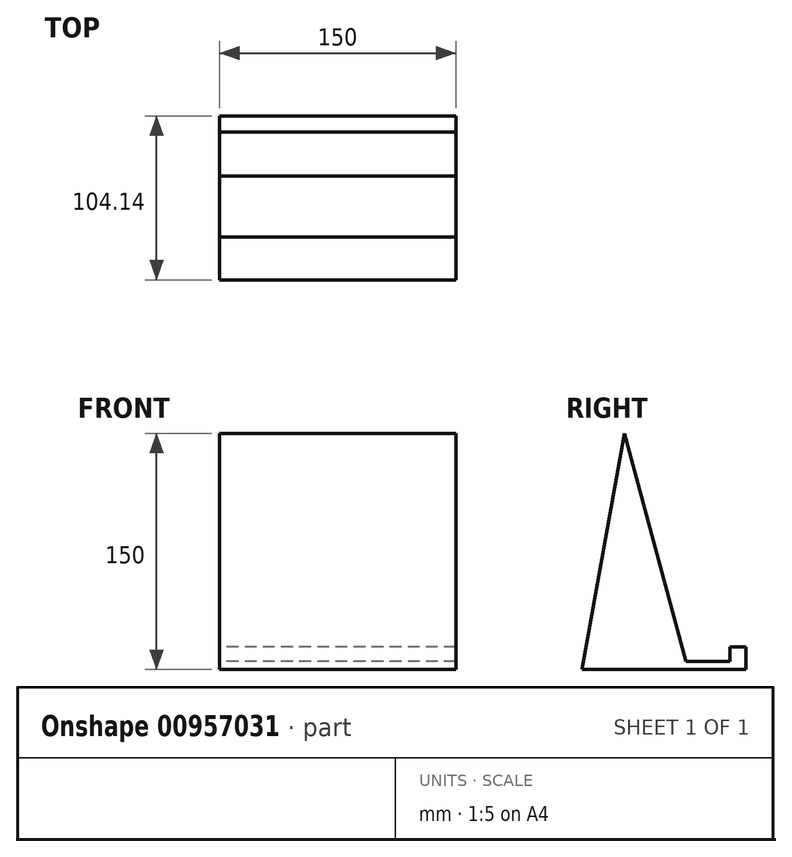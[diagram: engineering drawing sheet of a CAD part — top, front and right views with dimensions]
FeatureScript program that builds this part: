
annotation { "Feature Type Name" : "Feature", "Feature Type Description" : "" }
export const myFeature = defineFeature(function(context is Context, id is Id, definition is map)
    precondition{}
    {
        {
            var Q0;
            Q0=qCreatedBy(makeId("Right.planeOp"),FACE);
            var sketch = newSketch(context, id + "F0", { "sketchPlane" : qUnion([Q0])});
            skLineSegment(sketch, "E0", {"start": v(0, 150) * mm, "end": v(-27.16, 0) * mm});
            skLineSegment(sketch, "E1", {"start": v(-27.16, 0) * mm, "end": v(40.2, 0) * mm});
            skLineSegment(sketch, "E2", {"start": v(38.82, 5.11) * mm, "end": v(0, 150) * mm, "construction": true});
            skLineSegment(sketch, "E3", {"start": v(38.82, 5.11) * mm, "end": v(66.82, 5.11) * mm});
            skLineSegment(sketch, "E4", {"start": v(66.82, 5.11) * mm, "end": v(66.82, 14.36) * mm});
            skLineSegment(sketch, "E5", {"start": v(76.98, 0) * mm, "end": v(40.2, 0) * mm});
            skLineSegment(sketch, "E6", {"start": v(38.82, 5.11) * mm, "end": v(0, 150) * mm});
            skLineSegment(sketch, "E7", {"start": v(76.98, 0) * mm, "end": v(76.98, 14.36) * mm});
            skLineSegment(sketch, "E8", {"start": v(76.98, 14.36) * mm, "end": v(66.82, 14.36) * mm});
            skSolve(sketch);
        }
        {
            var Q0;
            Q0 = qSketchRegion(id + "F0", true);
            extrude(context, id + "F1", {"entities" : qUnion([Q0]), "depth" : 150 * mm, "offsetDistance" : 25.4 * mm});
        }
    });
